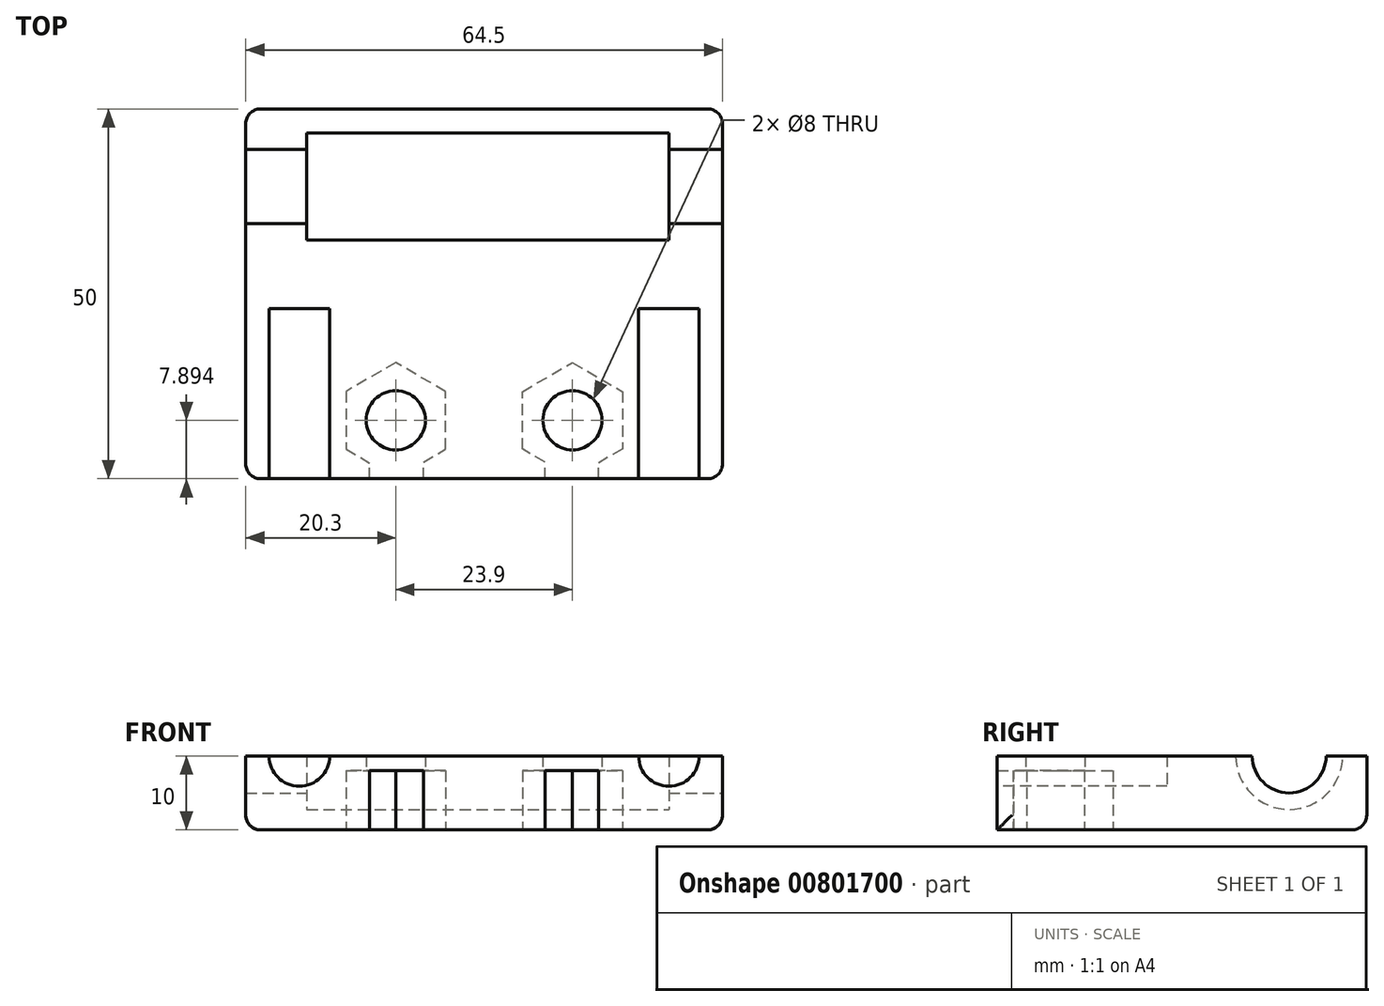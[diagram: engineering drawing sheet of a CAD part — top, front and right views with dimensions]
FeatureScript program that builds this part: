
annotation { "Feature Type Name" : "Feature", "Feature Type Description" : "" }
export const myFeature = defineFeature(function(context is Context, id is Id, definition is map)
    precondition{}
    {
        {
            var Q0;
            Q0=qCreatedBy(makeId("Top.planeOp"),FACE);
            var sketch = newSketch(context, id + "F0", { "sketchPlane" : qUnion([Q0])});
            skLineSegment(sketch, "E0.bottom", {"start": v(32.25, 25) * mm, "end": v(-32.25, 25) * mm});
            skLineSegment(sketch, "E0.top", {"start": v(32.25, -25) * mm, "end": v(-32.25, -25) * mm});
            skLineSegment(sketch, "E0.left", {"start": v(32.25, 25) * mm, "end": v(32.25, -25) * mm});
            skLineSegment(sketch, "E0.right", {"start": v(-32.25, 25) * mm, "end": v(-32.25, -25) * mm});
            skPoint(sketch, "E0.middle", {"position": v(0, 0) * mm});
            skSolve(sketch);
        }
        {
            var Q0;
            Q0=makeQuery(id+"F0.imprint","IMPRINT",FACE,{"disambiguationData":[TD([[makeQuery(id+"F0.imprint","IMPRINT",EDGE,{"derivedFrom":sQuery(id+"F0.wireOp",EDGE,"E0.bottom")}),1.0]])]});
            extrude(context, id + "F1", {"entities" : qUnion([Q0]), "depth" : 10 * mm, "offsetDistance" : 25 * mm});
        }
        {
            var Q0;
            Q0=makeQuery(id+"F1.opExtrude","CAP_FACE",FACE,{"disambiguationData":[OSD([sQuery(id+"F0.wireOp",EDGE,"E0.bottom"),sQuery(id+"F0.wireOp",EDGE,"E0.top"),sQuery(id+"F0.wireOp",EDGE,"E0.left"),sQuery(id+"F0.wireOp",EDGE,"E0.right")])],"isStart":true});
            var sketch = newSketch(context, id + "F2", { "sketchPlane" : qUnion([Q0])});
            skCircle(sketch, "E1.cCircle", {"center": v(-11.95, 17.1) * mm, "radius": 6.75 * mm, "construction": true});
            skLineSegment(sketch, "E1.0", {"start": v(-5.2, 21) * mm, "end": v(-5.2, 13.2) * mm});
            skLineSegment(sketch, "E1.1", {"start": v(-5.2, 13.2) * mm, "end": v(-11.95, 9.31) * mm});
            skLineSegment(sketch, "E1.2", {"start": v(-11.95, 9.31) * mm, "end": v(-18.7, 13.2) * mm});
            skLineSegment(sketch, "E1.3", {"start": v(-18.7, 13.2) * mm, "end": v(-18.7, 21) * mm});
            skLineSegment(sketch, "E1.4", {"start": v(-18.7, 21) * mm, "end": v(-11.95, 24.9) * mm});
            skLineSegment(sketch, "E1.5", {"start": v(-11.95, 24.9) * mm, "end": v(-5.2, 21) * mm});
            skPoint(sketch, "E1.0.midPoint", {"position": v(-5.2, 17.1) * mm});
            skLineSegment(sketch, "E2.MirrorCS", {"start": v(11.95, 24.9) * mm, "end": v(5.2, 21) * mm});
            skLineSegment(sketch, "E3.MirrorCS", {"start": v(18.7, 21) * mm, "end": v(11.95, 24.9) * mm});
            skLineSegment(sketch, "E4.MirrorCS", {"start": v(18.7, 13.2) * mm, "end": v(18.7, 21) * mm});
            skLineSegment(sketch, "E5.MirrorCS", {"start": v(11.95, 9.31) * mm, "end": v(18.7, 13.2) * mm});
            skLineSegment(sketch, "E6.MirrorCS", {"start": v(5.2, 13.2) * mm, "end": v(11.95, 9.31) * mm});
            skLineSegment(sketch, "E7.MirrorCS", {"start": v(5.2, 21) * mm, "end": v(5.2, 13.2) * mm});
            skPoint(sketch, "E8.MirrorP", {"position": v(11.95, 17.1) * mm});
            skSolve(sketch);
        }
        {
            var Q0;
            Q0 = qSketchRegion(id + "F2", true);
            extrude(context, id + "F3", {"entities" : qUnion([Q0]), "operationType" : NewBodyOperationType.REMOVE, "oppositeDirection" : true, "depth" : 8 * mm, "offsetDistance" : 25 * mm});
        }
        {
            var Q0;
            Q0=makeQuery(id+"F3.boolean.opBoolean","COPY",FACE,{"derivedFrom":makeQuery(id+"F3.opExtrude","CAP_FACE",FACE,{"disambiguationData":[OSD([sQuery(id+"F2.wireOp",EDGE,"E1.0"),sQuery(id+"F2.wireOp",EDGE,"E1.1"),sQuery(id+"F2.wireOp",EDGE,"E1.2"),sQuery(id+"F2.wireOp",EDGE,"E1.3"),sQuery(id+"F2.wireOp",EDGE,"E1.4"),sQuery(id+"F2.wireOp",EDGE,"E1.5")])],"isStart":false})});
            var sketch = newSketch(context, id + "F4", { "sketchPlane" : qUnion([Q0])});
            skCircle(sketch, "E9", {"center": v(-11.95, 17.1) * mm, "radius": 4 * mm});
            skPoint(sketch, "E9.centerSnap0", {"position": v(-5.2, 17.1) * mm});
            skCircle(sketch, "E10.MirrorC", {"center": v(11.95, 17.1) * mm, "radius": 4 * mm});
            skSolve(sketch);
        }
        {
            var Q0;
            Q0 = qSketchRegion(id + "F4", true);
            extrude(context, id + "F5", {"entities" : qUnion([Q0]), "operationType" : NewBodyOperationType.REMOVE, "oppositeDirection" : true, "depth" : 25 * mm, "offsetDistance" : 25 * mm});
        }
        {
            var Q0;
            Q0=makeQuery(id+"F1.opExtrude","SWEPT_FACE",FACE,{"disambiguationData":[OSD([sQuery(id+"F0.wireOp",EDGE,"E0.top")])]});
            var sketch = newSketch(context, id + "F6", { "sketchPlane" : qUnion([Q0])});
            skCircle(sketch, "E11", {"center": v(25, 10) * mm, "radius": 4.1 * mm});
            skCircle(sketch, "E12.MirrorC", {"center": v(-25, 10) * mm, "radius": 4.1 * mm});
            skSolve(sketch);
        }
        {
            var Q0;
            Q0 = qSketchRegion(id + "F6", true);
            extrude(context, id + "F7", {"entities" : qUnion([Q0]), "operationType" : NewBodyOperationType.REMOVE, "oppositeDirection" : true, "depth" : 23 * mm, "offsetDistance" : 25 * mm});
        }
        {
            var Q0;
            Q0=makeQuery(id+"F1.opExtrude","SWEPT_FACE",FACE,{"disambiguationData":[OSD([sQuery(id+"F0.wireOp",EDGE,"E0.left")])]});
            var sketch = newSketch(context, id + "F8", { "sketchPlane" : qUnion([Q0])});
            skCircle(sketch, "E13", {"center": v(14.5, 10) * mm, "radius": 5 * mm});
            skSolve(sketch);
        }
        {
            var Q0;
            Q0 = qSketchRegion(id + "F8", true);
            extrude(context, id + "F9", {"entities" : qUnion([Q0]), "operationType" : NewBodyOperationType.REMOVE, "endBound" : BoundingType.THROUGH_ALL, "oppositeDirection" : true, "depth" : 25 * mm, "offsetDistance" : 25 * mm});
        }
        {
            var Q0;
            Q0=qCreatedBy(makeId("Right.planeOp"),FACE);
            var sketch = newSketch(context, id + "F10", { "sketchPlane" : qUnion([Q0])});
            skArc(sketch, "E14.0", {"start": v(9.5, 10) * mm, "mid": v(14.5, 5) * mm, "end": v(19.5, 10) * mm, "construction": true});
            skCircle(sketch, "E15", {"center": v(14.5, 10) * mm, "radius": 7.23 * mm});
            skSolve(sketch);
        }
        {
            var Q0;
            Q0=makeQuery(id+"F10.imprint","IMPRINT",FACE,{"disambiguationData":[TD([[makeQuery(id+"F10.imprint","IMPRINT",EDGE,{"derivedFrom":sQuery(id+"F10.wireOp",EDGE,"E15")}),1.0]])]});
            var Q1;
            Q1=sQuery(id+"F10.wireOp",EDGE,"E14.0");
            extrude(context, id + "F11", {"entities" : qUnion([Q0]), "operationType" : NewBodyOperationType.REMOVE, "surfaceEntities" : qUnion([Q1]), "oppositeDirection" : true, "depth" : 24 * mm, "offsetDistance" : 25 * mm, "hasSecondDirection" : true, "secondDirectionOppositeDirection" : false, "secondDirectionDepth" : 25 * mm});
        }
        {
            var Q0;
            Q0=makeQuery(id+"F1.opExtrude","CAP_EDGE",EDGE,{"disambiguationData":[OSD([sQuery(id+"F0.wireOp",EDGE,"E0.bottom")])],"isStart":true});
            var Q1;
            Q1=makeQuery(id+"F1.opExtrude","CAP_EDGE",EDGE,{"disambiguationData":[OSD([sQuery(id+"F0.wireOp",EDGE,"E0.left")])],"isStart":true});
            var Q2;
            Q2=makeQuery(id+"F1.opExtrude","CAP_EDGE",EDGE,{"disambiguationData":[OSD([sQuery(id+"F0.wireOp",EDGE,"E0.right")])],"isStart":true});
            var Q3;
            Q3=makeQuery(id+"F1.opExtrude","SWEPT_EDGE",EDGE,{"disambiguationData":[OSD([sQuery(id+"F0.wireOp",EDGE,"E0.bottom"),sQuery(id+"F0.wireOp",EDGE,"E0.left")])]});
            var Q4;
            Q4=makeQuery(id+"F1.opExtrude","SWEPT_EDGE",EDGE,{"disambiguationData":[OSD([sQuery(id+"F0.wireOp",EDGE,"E0.bottom"),sQuery(id+"F0.wireOp",EDGE,"E0.right")])]});
            var Q5;
            Q5=makeQuery(id+"F1.opExtrude","SWEPT_EDGE",EDGE,{"disambiguationData":[OSD([sQuery(id+"F0.wireOp",EDGE,"E0.top"),sQuery(id+"F0.wireOp",EDGE,"E0.right")])]});
            var Q6;
            Q6=makeQuery(id+"F1.opExtrude","SWEPT_EDGE",EDGE,{"disambiguationData":[OSD([sQuery(id+"F0.wireOp",EDGE,"E0.top"),sQuery(id+"F0.wireOp",EDGE,"E0.left")])]});
            fillet(context, id + "F12", {"entities" : qUnion([Q0, Q1, Q2, Q3, Q4, Q5, Q6]), "radius" : 2 * mm, "tangentPropagation" : true, "allowEdgeOverflow" : false});
        }
        {
            var Q0;
            Q0=makeQuery(id+"F3.boolean.opBoolean","COPY",FACE,{"derivedFrom":makeQuery(id+"F3.opExtrude","CAP_FACE",FACE,{"disambiguationData":[OSD([sQuery(id+"F2.wireOp",EDGE,"E2.MirrorCS"),sQuery(id+"F2.wireOp",EDGE,"E3.MirrorCS"),sQuery(id+"F2.wireOp",EDGE,"E4.MirrorCS"),sQuery(id+"F2.wireOp",EDGE,"E5.MirrorCS"),sQuery(id+"F2.wireOp",EDGE,"E6.MirrorCS"),sQuery(id+"F2.wireOp",EDGE,"E7.MirrorCS")])],"isStart":false})});
            var sketch = newSketch(context, id + "F13", { "sketchPlane" : qUnion([Q0])});
            skLineSegment(sketch, "E16.bottom", {"start": v(-8.23, 27.76) * mm, "end": v(-15.47, 27.76) * mm});
            skLineSegment(sketch, "E16.top", {"start": v(-8.23, 22.03) * mm, "end": v(-15.47, 22.03) * mm});
            skLineSegment(sketch, "E16.left", {"start": v(-8.23, 27.76) * mm, "end": v(-8.23, 22.03) * mm});
            skLineSegment(sketch, "E16.right", {"start": v(-15.47, 27.76) * mm, "end": v(-15.47, 22.03) * mm});
            skPoint(sketch, "E16.middle", {"position": v(-11.85, 24.9) * mm});
            skLineSegment(sketch, "E17.MirrorCS", {"start": v(8.23, 27.76) * mm, "end": v(15.47, 27.76) * mm});
            skLineSegment(sketch, "E18.MirrorCS", {"start": v(15.47, 27.76) * mm, "end": v(15.47, 22.03) * mm});
            skLineSegment(sketch, "E19.MirrorCS", {"start": v(8.23, 22.03) * mm, "end": v(15.47, 22.03) * mm});
            skLineSegment(sketch, "E20.MirrorCS", {"start": v(8.23, 27.76) * mm, "end": v(8.23, 22.03) * mm});
            skSolve(sketch);
        }
        {
            var Q0;
            Q0=makeQuery(id+"F13.imprint","IMPRINT",FACE,{"disambiguationData":[TD([[makeQuery(id+"F13.imprint","IMPRINT",EDGE,{"derivedFrom":sQuery(id+"F13.wireOp",EDGE,"E16.bottom")}),1.0]])]});
            var Q1;
            {var subQ6=sQuery(id+"F13.wireOp",EDGE,"E17.MirrorCS");Q1=makeQuery(id+"F13.imprint","IMPRINT",FACE,{"disambiguationData":[TD([[makeQuery(id+"F13.imprint","IMPRINT",EDGE,{"derivedFrom":subQ6}),-1.0]])]});}
            extrude(context, id + "F14", {"entities" : qUnion([Q0, Q1]), "operationType" : NewBodyOperationType.REMOVE, "depth" : 25 * mm, "offsetDistance" : 25 * mm});
        }
    });
